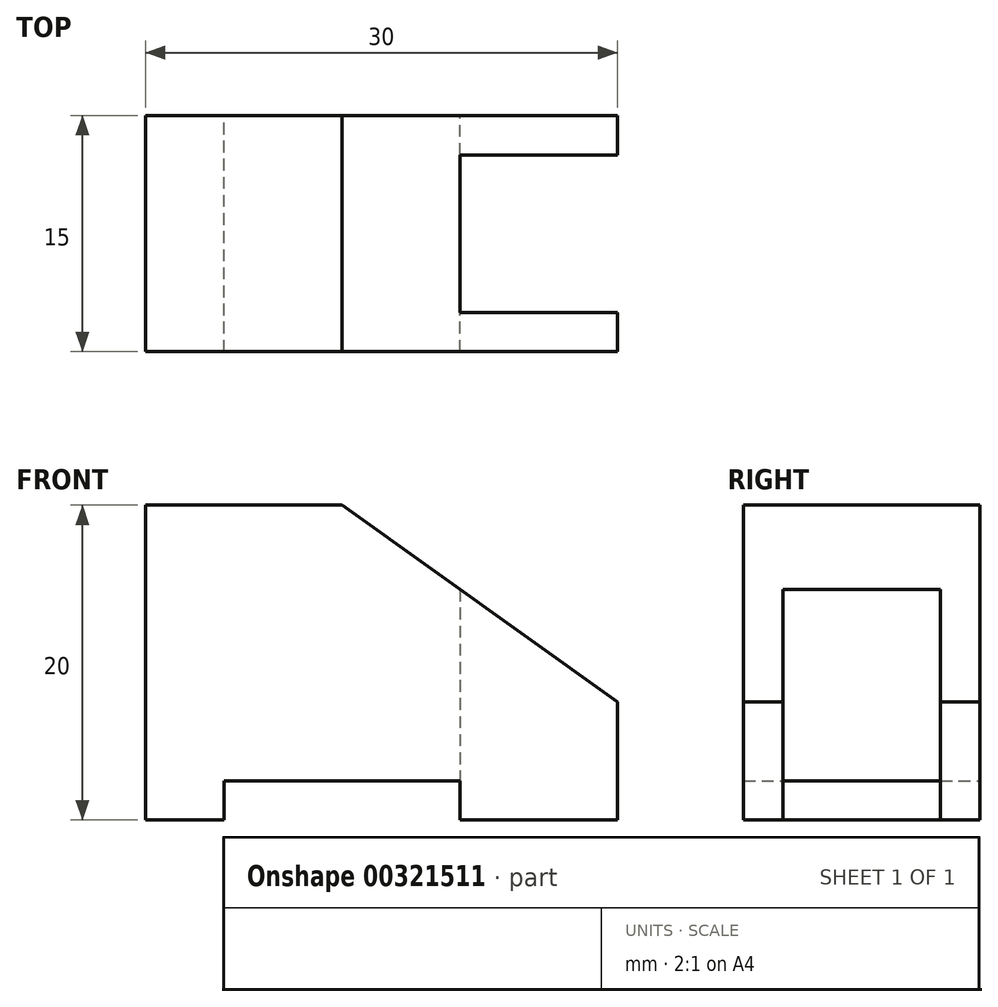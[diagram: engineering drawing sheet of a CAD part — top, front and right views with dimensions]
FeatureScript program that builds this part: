
annotation { "Feature Type Name" : "Feature", "Feature Type Description" : "" }
export const myFeature = defineFeature(function(context is Context, id is Id, definition is map)
    precondition{}
    {
        {
            var Q0;
            Q0=qCreatedBy(makeId("Front.planeOp"),FACE);
            var sketch = newSketch(context, id + "F0", { "sketchPlane" : qUnion([Q0])});
            skLineSegment(sketch, "E0", {"start": v(0, 0) * mm, "end": v(0, 20) * mm});
            skLineSegment(sketch, "E1", {"start": v(0, 20) * mm, "end": v(12.5, 20) * mm});
            skLineSegment(sketch, "E2", {"start": v(12.5, 20) * mm, "end": v(30, 7.5) * mm});
            skLineSegment(sketch, "E3", {"start": v(30, 7.5) * mm, "end": v(30, 0) * mm});
            skLineSegment(sketch, "E4", {"start": v(30, 0) * mm, "end": v(20, 0) * mm});
            skLineSegment(sketch, "E5", {"start": v(20, 0) * mm, "end": v(20, 2.5) * mm});
            skLineSegment(sketch, "E6", {"start": v(20, 2.5) * mm, "end": v(5, 2.5) * mm});
            skLineSegment(sketch, "E7", {"start": v(5, 2.5) * mm, "end": v(5, 0) * mm});
            skLineSegment(sketch, "E8", {"start": v(5, 0) * mm, "end": v(0, 0) * mm});
            skSolve(sketch);
        }
        {
            var Q0;
            Q0 = qSketchRegion(id + "F0", true);
            extrude(context, id + "F1", {"entities" : qUnion([Q0]), "depth" : 15 * mm});
        }
        {
            var Q0;
            Q0=makeQuery(id+"F1.opExtrude","SWEPT_FACE",FACE,{"disambiguationData":[OSD([sQuery(id+"F0.wireOp",EDGE,"E4")])]});
            var sketch = newSketch(context, id + "F2", { "sketchPlane" : qUnion([Q0])});
            skLineSegment(sketch, "E9", {"start": v(20, 12.5) * mm, "end": v(20, 2.5) * mm});
            skLineSegment(sketch, "E10", {"start": v(20, 12.5) * mm, "end": v(30, 12.5) * mm});
            skLineSegment(sketch, "E11", {"start": v(20, 2.5) * mm, "end": v(30, 2.5) * mm});
            skLineSegment(sketch, "E12", {"start": v(30, 12.5) * mm, "end": v(30, 2.5) * mm});
            skSolve(sketch);
        }
        {
            var Q0;
            Q0=makeQuery(id+"F2.imprint","IMPRINT",FACE,{"disambiguationData":[TD([[makeQuery(id+"F2.imprint","IMPRINT",EDGE,{"derivedFrom":sQuery(id+"F2.wireOp",EDGE,"E9")}),1.0]])]});
            extrude(context, id + "F3", {"entities" : qUnion([Q0]), "operationType" : NewBodyOperationType.REMOVE, "oppositeDirection" : true, "depth" : 25 * mm});
        }
    });
